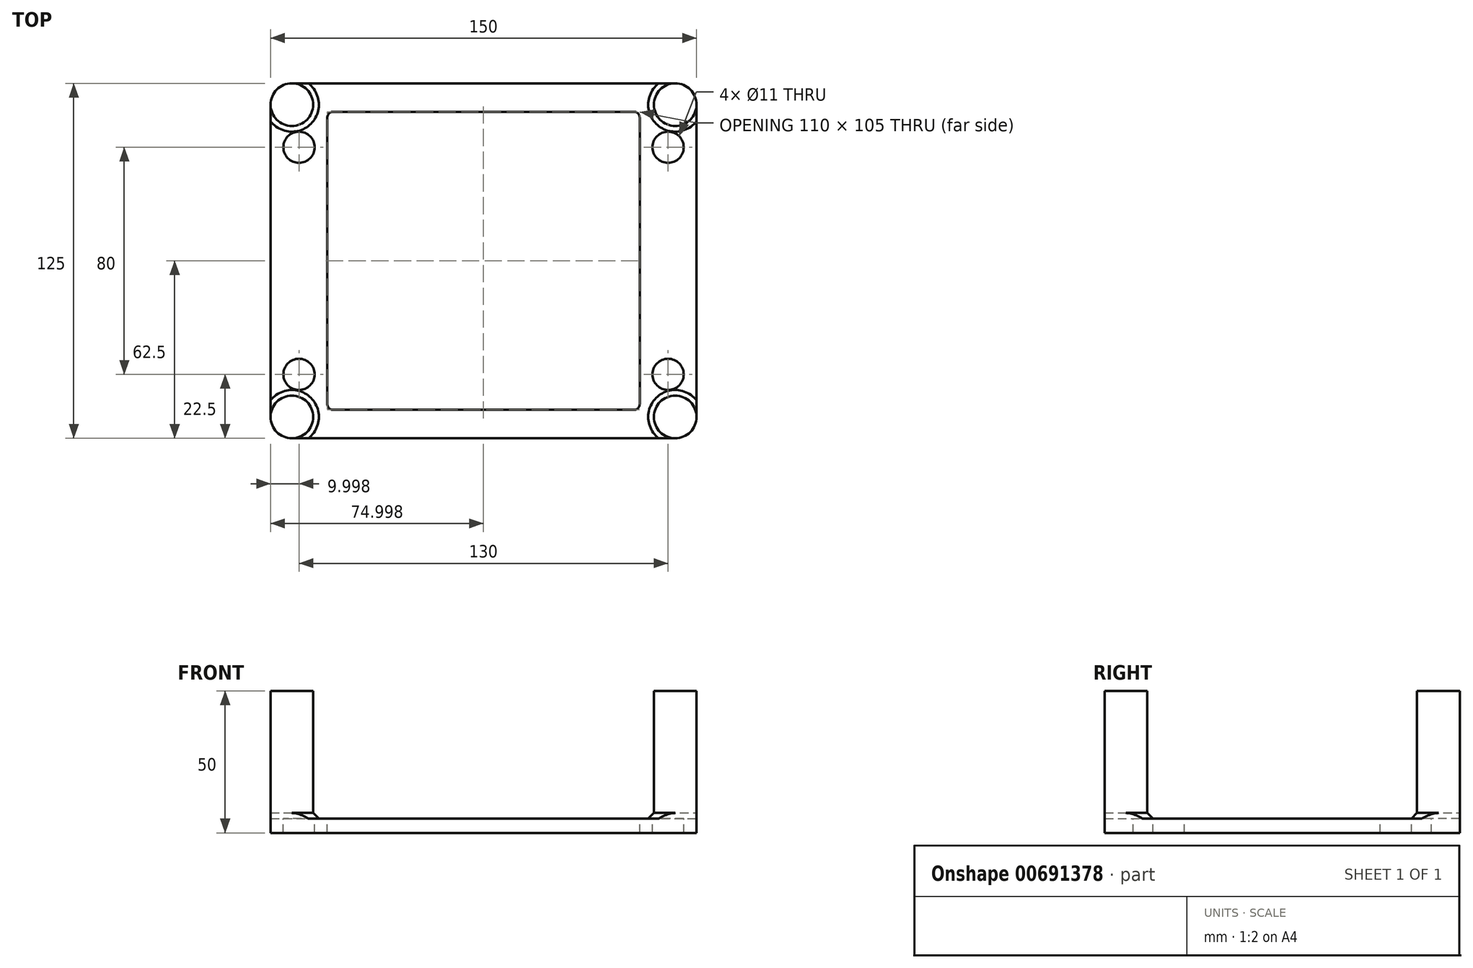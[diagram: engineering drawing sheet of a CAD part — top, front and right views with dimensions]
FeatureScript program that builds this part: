
annotation { "Feature Type Name" : "Feature", "Feature Type Description" : "" }
export const myFeature = defineFeature(function(context is Context, id is Id, definition is map)
    precondition{}
    {
        {
            var Q0;
            Q0=qCreatedBy(makeId("Top.planeOp"),FACE);
            var sketch = newSketch(context, id + "F0", { "sketchPlane" : qUnion([Q0])});
            skLineSegment(sketch, "E0.bottom", {"start": v(-80.74, 65.9) * mm, "end": v(69.26, 65.9) * mm});
            skLineSegment(sketch, "E0.top", {"start": v(-80.74, -59.1) * mm, "end": v(69.26, -59.1) * mm});
            skLineSegment(sketch, "E0.left", {"start": v(-80.74, 65.9) * mm, "end": v(-80.74, -59.1) * mm});
            skLineSegment(sketch, "E0.right", {"start": v(69.26, 65.9) * mm, "end": v(69.26, -59.1) * mm});
            skPoint(sketch, "E1", {"position": v(-70.74, 43.4) * mm});
            skPoint(sketch, "E2", {"position": v(-70.74, -36.6) * mm});
            skPoint(sketch, "E3", {"position": v(59.26, -36.6) * mm});
            skPoint(sketch, "E4", {"position": v(59.26, 43.4) * mm});
            skLineSegment(sketch, "E5.bottom", {"start": v(-60.74, 55.9) * mm, "end": v(49.26, 55.9) * mm});
            skLineSegment(sketch, "E5.top", {"start": v(-60.74, -49.1) * mm, "end": v(49.26, -49.1) * mm});
            skLineSegment(sketch, "E5.left", {"start": v(-60.74, 55.9) * mm, "end": v(-60.74, -49.1) * mm});
            skLineSegment(sketch, "E5.right", {"start": v(49.26, 55.9) * mm, "end": v(49.26, -49.1) * mm});
            skCircle(sketch, "E6", {"center": v(-73.24, 58.4) * mm, "radius": 7.5 * mm});
            skCircle(sketch, "E7", {"center": v(-73.24, -51.6) * mm, "radius": 7.5 * mm});
            skCircle(sketch, "E8", {"center": v(61.76, 58.4) * mm, "radius": 7.5 * mm});
            skCircle(sketch, "E9", {"center": v(61.76, -51.6) * mm, "radius": 7.5 * mm});
            skSolve(sketch);
        }
        {
            var Q0;
            Q0=makeQuery(id+"F0.imprint","IMPRINT",FACE,{"disambiguationData":[TD([[makeQuery(id+"F0.imprint","IMPRINT",EDGE,{"derivedFrom":sQuery(id+"F0.wireOp",EDGE,"E0.bottom")}),-1.0]])]});
            var Q1;
            {var subQ5=sQuery(id+"F0.wireOp",EDGE,"E5.right");Q1=makeQuery(id+"F0.imprint","IMPRINT",FACE,{"disambiguationData":[TD([[makeQuery(id+"F0.imprint","IMPRINT",EDGE,{"derivedFrom":subQ5}),1.0]])]});}
            var Q2;
            {var subQ5=sQuery(id+"F0.wireOp",EDGE,"E5.bottom");Q2=makeQuery(id+"F0.imprint","IMPRINT",FACE,{"disambiguationData":[TD([[makeQuery(id+"F0.imprint","IMPRINT",EDGE,{"derivedFrom":subQ5}),1.0]])]});}
            var Q3;
            {var subQ5=sQuery(id+"F0.wireOp",EDGE,"E5.left");Q3=makeQuery(id+"F0.imprint","IMPRINT",FACE,{"disambiguationData":[TD([[makeQuery(id+"F0.imprint","IMPRINT",EDGE,{"derivedFrom":subQ5}),-1.0]])]});}
            var Q4;
            {var subQ5=sQuery(id+"F0.wireOp",EDGE,"E5.top");Q4=makeQuery(id+"F0.imprint","IMPRINT",FACE,{"disambiguationData":[TD([[makeQuery(id+"F0.imprint","IMPRINT",EDGE,{"derivedFrom":subQ5}),-1.0]])]});}
            var Q5;
            {var subQ0=sQuery(id+"F0.wireOp",EDGE,"E9");var subQ3=makeQuery(id+"F0.imprint","INTERSECT",VERTEX,{"derivedFrom":[sQuery(id+"F0.wireOp",EDGE,"E0.top"),subQ0]});Q5=makeQuery(id+"F0.imprint","IMPRINT",FACE,{"disambiguationData":[TD([[makeQuery(id+"F0.imprint","IMPRINT",EDGE,{"disambiguationData":[TD([[subQ3,-1.0]])],"derivedFrom":subQ0}),1.0]])]});}
            var Q6;
            {var subQ0=sQuery(id+"F0.wireOp",EDGE,"E7");var subQ3=makeQuery(id+"F0.imprint","INTERSECT",VERTEX,{"derivedFrom":[sQuery(id+"F0.wireOp",EDGE,"E0.top"),subQ0]});Q6=makeQuery(id+"F0.imprint","IMPRINT",FACE,{"disambiguationData":[TD([[makeQuery(id+"F0.imprint","IMPRINT",EDGE,{"disambiguationData":[TD([[subQ3,1.0]])],"derivedFrom":subQ0}),1.0]])]});}
            var Q7;
            {var subQ0=sQuery(id+"F0.wireOp",EDGE,"E8");var subQ1=makeQuery(id+"F0.imprint","INTERSECT",VERTEX,{"derivedFrom":[sQuery(id+"F0.wireOp",EDGE,"E0.bottom"),subQ0]});Q7=makeQuery(id+"F0.imprint","IMPRINT",FACE,{"disambiguationData":[TD([[makeQuery(id+"F0.imprint","IMPRINT",EDGE,{"disambiguationData":[TD([[subQ1,1.0]])],"derivedFrom":subQ0}),1.0]])]});}
            var Q8;
            {var subQ0=sQuery(id+"F0.wireOp",EDGE,"E6");var subQ2=makeQuery(id+"F0.imprint","INTERSECT",VERTEX,{"derivedFrom":[sQuery(id+"F0.wireOp",EDGE,"E0.bottom"),subQ0]});Q8=makeQuery(id+"F0.imprint","IMPRINT",FACE,{"disambiguationData":[TD([[makeQuery(id+"F0.imprint","IMPRINT",EDGE,{"disambiguationData":[TD([[subQ2,-1.0]])],"derivedFrom":subQ0}),1.0]])]});}
            var Q9;
            {var subQ0=sQuery(id+"F0.wireOp",EDGE,"E0.left");var subQ1=sQuery(id+"F0.wireOp",EDGE,"E0.top");var subQ2=makeQuery(id+"F0.imprint","INTERSECT",VERTEX,{"derivedFrom":[subQ1,subQ0]});Q9=makeQuery(id+"F0.imprint","IMPRINT",FACE,{"disambiguationData":[TD([[makeQuery(id+"F0.imprint","IMPRINT",EDGE,{"disambiguationData":[TD([[subQ2,-1.0]])],"derivedFrom":subQ1}),1.0]])]});}
            var Q10;
            {var subQ0=sQuery(id+"F0.wireOp",EDGE,"E0.right");var subQ1=sQuery(id+"F0.wireOp",EDGE,"E0.top");var subQ2=makeQuery(id+"F0.imprint","INTERSECT",VERTEX,{"derivedFrom":[subQ1,subQ0]});Q10=makeQuery(id+"F0.imprint","IMPRINT",FACE,{"disambiguationData":[TD([[makeQuery(id+"F0.imprint","IMPRINT",EDGE,{"disambiguationData":[TD([[subQ2,1.0]])],"derivedFrom":subQ1}),1.0]])]});}
            extrude(context, id + "F1", {"entities" : qUnion([Q0, Q1, Q2, Q3, Q4, Q5, Q6, Q7, Q8, Q9, Q10]), "oppositeDirection" : true, "depth" : 5 * mm, "offsetDistance" : 25 * mm});
        }
        {
            var Q0;
            {var subQ0=sQuery(id+"F0.wireOp",EDGE,"E9");var subQ3=makeQuery(id+"F0.imprint","INTERSECT",VERTEX,{"derivedFrom":[sQuery(id+"F0.wireOp",EDGE,"E0.top"),subQ0]});Q0=makeQuery(id+"F0.imprint","IMPRINT",FACE,{"disambiguationData":[TD([[makeQuery(id+"F0.imprint","IMPRINT",EDGE,{"disambiguationData":[TD([[subQ3,-1.0]])],"derivedFrom":subQ0}),1.0]])]});}
            var Q1;
            {var subQ0=sQuery(id+"F0.wireOp",EDGE,"E8");var subQ1=makeQuery(id+"F0.imprint","INTERSECT",VERTEX,{"derivedFrom":[sQuery(id+"F0.wireOp",EDGE,"E0.bottom"),subQ0]});Q1=makeQuery(id+"F0.imprint","IMPRINT",FACE,{"disambiguationData":[TD([[makeQuery(id+"F0.imprint","IMPRINT",EDGE,{"disambiguationData":[TD([[subQ1,1.0]])],"derivedFrom":subQ0}),1.0]])]});}
            var Q2;
            {var subQ0=sQuery(id+"F0.wireOp",EDGE,"E7");var subQ3=makeQuery(id+"F0.imprint","INTERSECT",VERTEX,{"derivedFrom":[sQuery(id+"F0.wireOp",EDGE,"E0.top"),subQ0]});Q2=makeQuery(id+"F0.imprint","IMPRINT",FACE,{"disambiguationData":[TD([[makeQuery(id+"F0.imprint","IMPRINT",EDGE,{"disambiguationData":[TD([[subQ3,1.0]])],"derivedFrom":subQ0}),1.0]])]});}
            var Q3;
            {var subQ0=sQuery(id+"F0.wireOp",EDGE,"E6");var subQ2=makeQuery(id+"F0.imprint","INTERSECT",VERTEX,{"derivedFrom":[sQuery(id+"F0.wireOp",EDGE,"E0.bottom"),subQ0]});Q3=makeQuery(id+"F0.imprint","IMPRINT",FACE,{"disambiguationData":[TD([[makeQuery(id+"F0.imprint","IMPRINT",EDGE,{"disambiguationData":[TD([[subQ2,-1.0]])],"derivedFrom":subQ0}),1.0]])]});}
            extrude(context, id + "F2", {"entities" : qUnion([Q0, Q1, Q2, Q3]), "operationType" : NewBodyOperationType.ADD, "depth" : 45 * mm, "offsetDistance" : 25 * mm});
        }
        {
            var Q0;
            Q0=sQuery(id+"F0.wireOp",VERTEX,"E1");
            var Q1;
            Q1=sQuery(id+"F0.wireOp",VERTEX,"E2");
            var Q2;
            Q2=sQuery(id+"F0.wireOp",VERTEX,"E4");
            var Q3;
            Q3=sQuery(id+"F0.wireOp",VERTEX,"E3");
            var Q4;
            Q4=makeQuery(id+"F1.opExtrude","SWEPT_BODY",BODY,{"disambiguationData":[OSD([sQuery(id+"F0.wireOp",EDGE,"E0.bottom"),sQuery(id+"F0.wireOp",EDGE,"E0.top"),sQuery(id+"F0.wireOp",EDGE,"E0.left"),sQuery(id+"F0.wireOp",EDGE,"E0.right"),sQuery(id+"F0.wireOp",EDGE,"E5.bottom"),sQuery(id+"F0.wireOp",EDGE,"E5.top"),sQuery(id+"F0.wireOp",EDGE,"E5.left"),sQuery(id+"F0.wireOp",EDGE,"E5.right")])]});
            hole(context, id + "F3", {"style" : HoleStyle.SIMPLE, "endStyle" : HoleEndStyle.THROUGH, "holeDiameter" : 11 * mm, "majorDiameter" : 5 * mm, "isTappedThrough" : true, "tappedDepth" : 12 * mm, "tapClearance" : 3, "locations" : qUnion([Q0, Q1, Q2, Q3]), "scope" : qUnion([Q4])});
        }
        {
            var Q0;
            Q0=makeQuery(id+"F1.opExtrude","SWEPT_EDGE",EDGE,{"disambiguationData":[OSD([sQuery(id+"F0.wireOp",EDGE,"E0.bottom"),sQuery(id+"F0.wireOp",EDGE,"E0.right")])]});
            var Q1;
            Q1=makeQuery(id+"F1.opExtrude","SWEPT_EDGE",EDGE,{"disambiguationData":[OSD([sQuery(id+"F0.wireOp",EDGE,"E0.top"),sQuery(id+"F0.wireOp",EDGE,"E0.right")])]});
            var Q2;
            Q2=makeQuery(id+"F1.opExtrude","SWEPT_EDGE",EDGE,{"disambiguationData":[OSD([sQuery(id+"F0.wireOp",EDGE,"E0.top"),sQuery(id+"F0.wireOp",EDGE,"E0.left")])]});
            var Q3;
            Q3=makeQuery(id+"F1.opExtrude","SWEPT_EDGE",EDGE,{"disambiguationData":[OSD([sQuery(id+"F0.wireOp",EDGE,"E0.bottom"),sQuery(id+"F0.wireOp",EDGE,"E0.left")])]});
            fillet(context, id + "F4", {"entities" : qUnion([Q0, Q1, Q2, Q3]), "radius" : 7.5 * mm, "tangentPropagation" : true, "allowEdgeOverflow" : false});
        }
        {
            var Q0;
            Q0=makeQuery(id+"F1.opExtrude","SWEPT_EDGE",EDGE,{"disambiguationData":[OSD([sQuery(id+"F0.wireOp",EDGE,"E5.bottom"),sQuery(id+"F0.wireOp",EDGE,"E5.left")])]});
            var Q1;
            Q1=makeQuery(id+"F1.opExtrude","SWEPT_EDGE",EDGE,{"disambiguationData":[OSD([sQuery(id+"F0.wireOp",EDGE,"E5.bottom"),sQuery(id+"F0.wireOp",EDGE,"E5.right")])]});
            var Q2;
            Q2=makeQuery(id+"F1.opExtrude","SWEPT_EDGE",EDGE,{"disambiguationData":[OSD([sQuery(id+"F0.wireOp",EDGE,"E5.top"),sQuery(id+"F0.wireOp",EDGE,"E5.left")])]});
            var Q3;
            Q3=makeQuery(id+"F1.opExtrude","SWEPT_EDGE",EDGE,{"disambiguationData":[OSD([sQuery(id+"F0.wireOp",EDGE,"E5.top"),sQuery(id+"F0.wireOp",EDGE,"E5.right")])]});
            fillet(context, id + "F5", {"entities" : qUnion([Q0, Q1, Q2, Q3]), "radius" : 2 * mm, "tangentPropagation" : true, "allowEdgeOverflow" : false});
        }
        {
            var Q0;
            Q0=makeQuery(id+"F2.boolean.opBoolean","SPLIT",EDGE,{"disambiguationData":[OD(1.0)],"derivedFrom":makeQuery(id+"F2.opExtrude","CAP_EDGE",EDGE,{"disambiguationData":[OSD([sQuery(id+"F0.wireOp",EDGE,"E8")])],"isStart":true})});
            var Q1;
            Q1=makeQuery(id+"F2.boolean.opBoolean","SPLIT",EDGE,{"disambiguationData":[OD(1.0)],"derivedFrom":makeQuery(id+"F2.opExtrude","CAP_EDGE",EDGE,{"disambiguationData":[OSD([sQuery(id+"F0.wireOp",EDGE,"E6")])],"isStart":true})});
            var Q2;
            Q2=makeQuery(id+"F2.boolean.opBoolean","SPLIT",EDGE,{"disambiguationData":[OD(1.0)],"derivedFrom":makeQuery(id+"F2.opExtrude","CAP_EDGE",EDGE,{"disambiguationData":[OSD([sQuery(id+"F0.wireOp",EDGE,"E9")])],"isStart":true})});
            var Q3;
            Q3=makeQuery(id+"F2.boolean.opBoolean","SPLIT",EDGE,{"disambiguationData":[OD(1.0)],"derivedFrom":makeQuery(id+"F2.opExtrude","CAP_EDGE",EDGE,{"disambiguationData":[OSD([sQuery(id+"F0.wireOp",EDGE,"E7")])],"isStart":true})});
            chamfer(context, id + "F6", {"entities" : qUnion([Q0, Q1, Q2, Q3]), "width" : 2 * mm, "tangentPropagation" : true});
        }
    });
